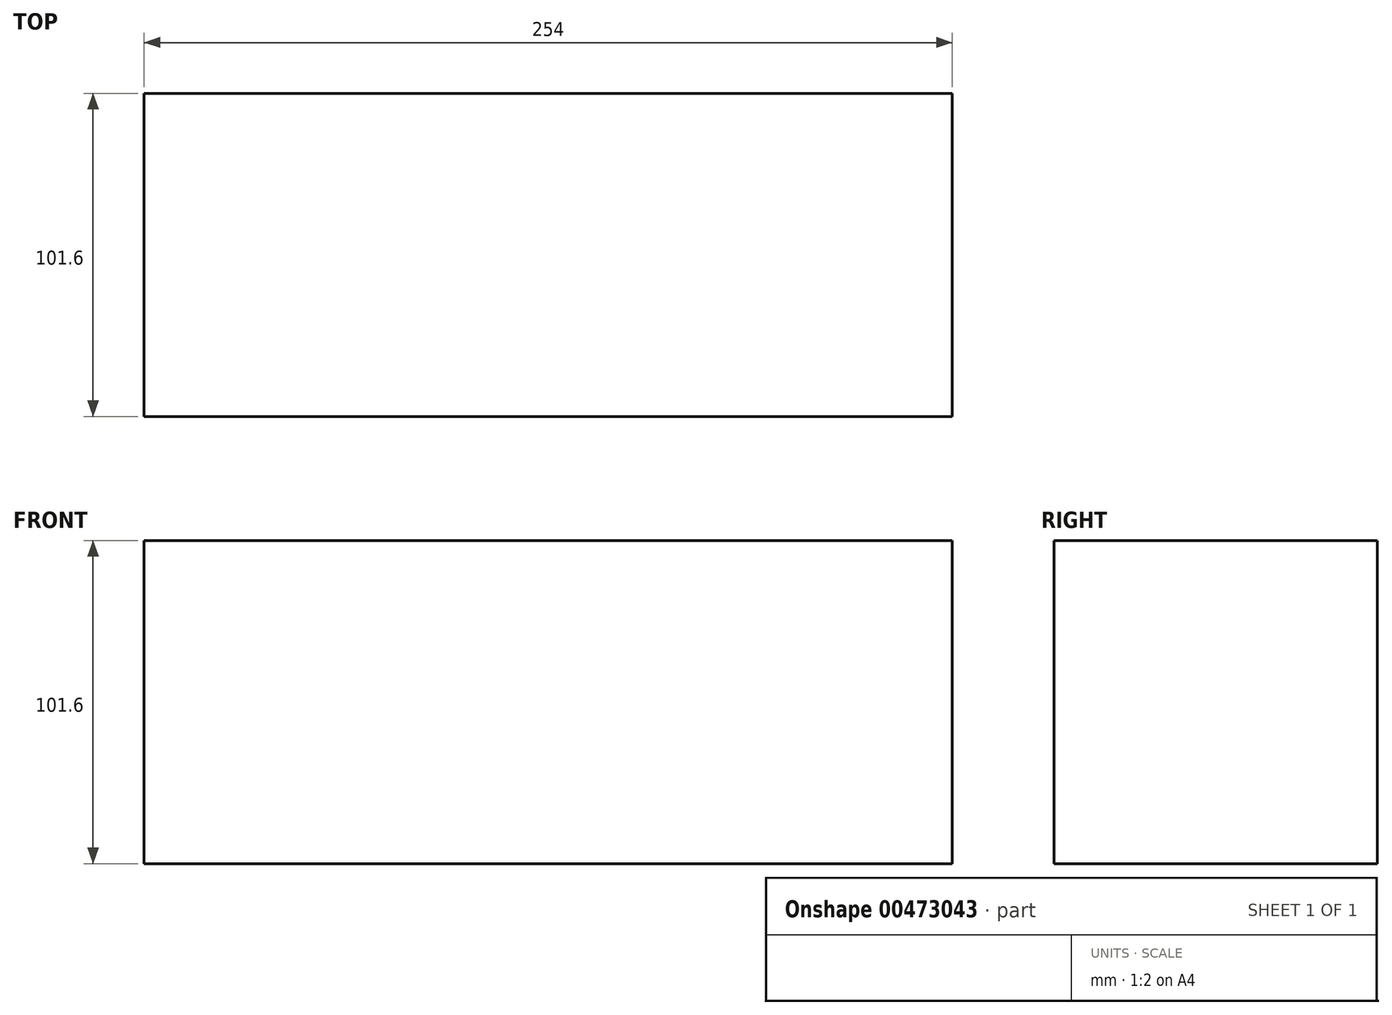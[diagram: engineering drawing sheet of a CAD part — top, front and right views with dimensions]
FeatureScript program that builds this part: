
annotation { "Feature Type Name" : "Feature", "Feature Type Description" : "" }
export const myFeature = defineFeature(function(context is Context, id is Id, definition is map)
    precondition{}
    {
        {
            var Q0;
            Q0=qCreatedBy(makeId("Front.planeOp"),FACE);
            var sketch = newSketch(context, id + "F0", { "sketchPlane" : qUnion([Q0])});
            skLineSegment(sketch, "E0.bottom", {"start": v(127, 50.8) * mm, "end": v(-127, 50.8) * mm});
            skLineSegment(sketch, "E0.top", {"start": v(127, -50.8) * mm, "end": v(-127, -50.8) * mm});
            skLineSegment(sketch, "E0.left", {"start": v(127, 50.8) * mm, "end": v(127, -50.8) * mm});
            skLineSegment(sketch, "E0.right", {"start": v(-127, 50.8) * mm, "end": v(-127, -50.8) * mm});
            skPoint(sketch, "E0.middle", {"position": v(0, 0) * mm});
            skSolve(sketch);
        }
        {
            var Q0;
            Q0=makeQuery(id+"F0.imprint","IMPRINT",FACE,{"disambiguationData":[TD([[makeQuery(id+"F0.imprint","IMPRINT",EDGE,{"derivedFrom":sQuery(id+"F0.wireOp",EDGE,"E0.bottom")}),1.0]])]});
            extrude(context, id + "F1", {"entities" : qUnion([Q0]), "depth" : 101.6 * mm});
        }
    });
